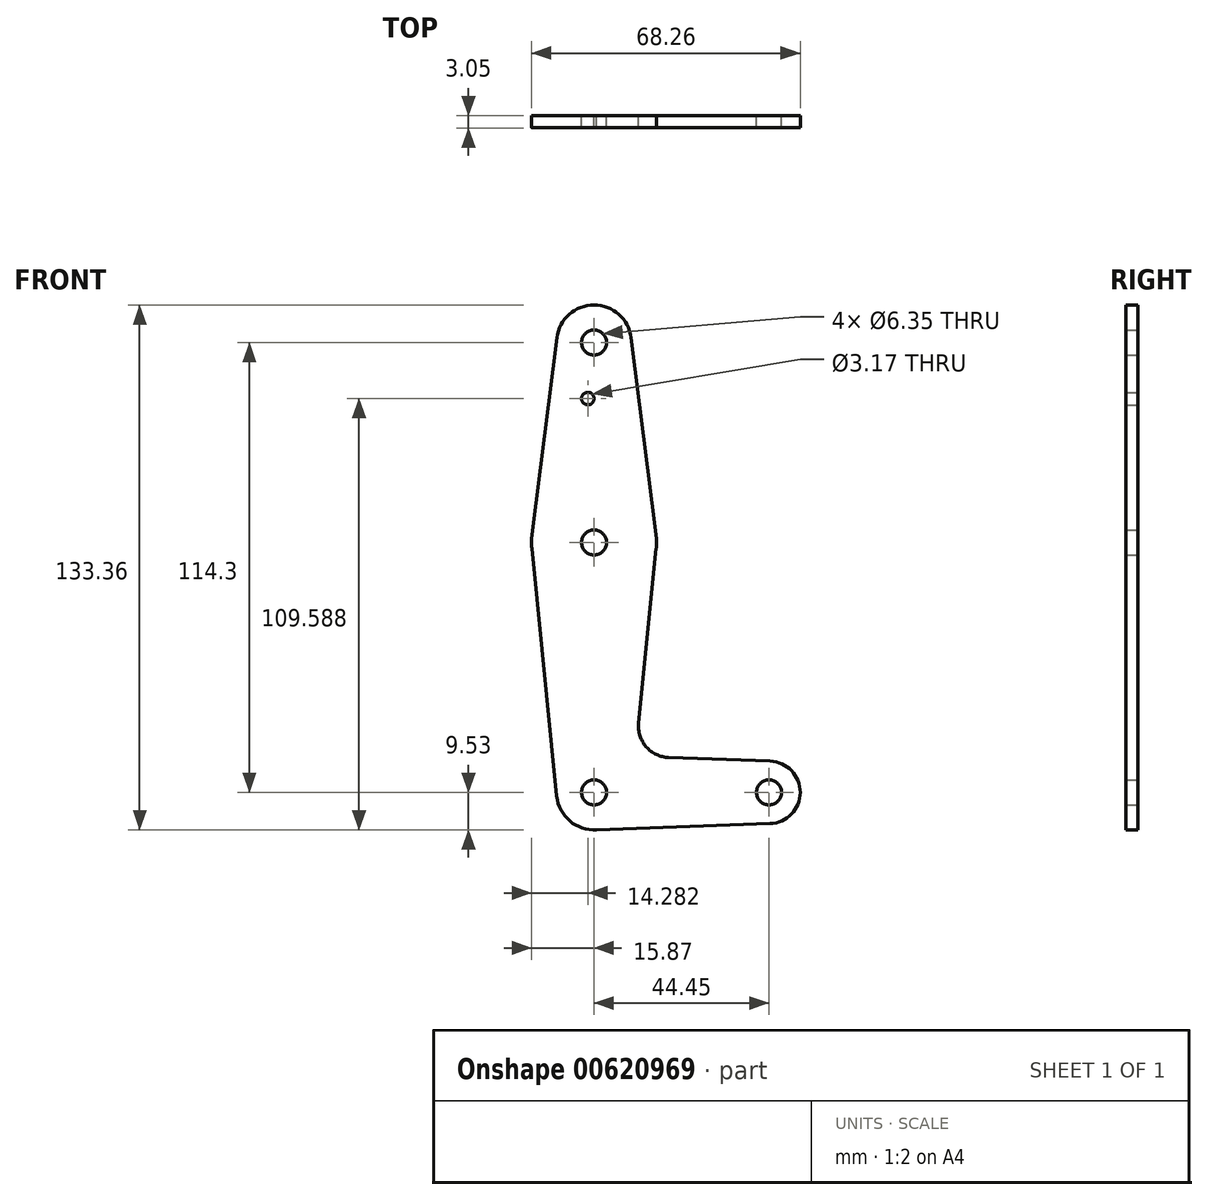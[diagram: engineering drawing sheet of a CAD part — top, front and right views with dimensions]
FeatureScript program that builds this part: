
annotation { "Feature Type Name" : "Feature", "Feature Type Description" : "" }
export const myFeature = defineFeature(function(context is Context, id is Id, definition is map)
    precondition{}
    {
        {
            var Q0;
            Q0=qCreatedBy(makeId("Front.planeOp"),FACE);
            var sketch = newSketch(context, id + "F0", { "sketchPlane" : qUnion([Q0])});
            skLineSegment(sketch, "E0", {"start": v(0, 0) * mm, "end": v(0, 114.3) * mm});
            skLineSegment(sketch, "E1", {"start": v(0, 114.3) * mm, "end": v(0, 0) * mm, "construction": true});
            skLineSegment(sketch, "E2", {"start": v(0, 0) * mm, "end": v(44.45, 0) * mm, "construction": true});
            skCircle(sketch, "E3", {"center": v(0, 0) * mm, "radius": 9.53 * mm});
            skCircle(sketch, "E4", {"center": v(0, 63.5) * mm, "radius": 15.88 * mm});
            skCircle(sketch, "E5", {"center": v(0, 114.3) * mm, "radius": 9.53 * mm});
            skCircle(sketch, "E6", {"center": v(44.45, 0) * mm, "radius": 7.94 * mm});
            skLineSegment(sketch, "E7", {"start": v(18.97, 8.85) * mm, "end": v(44.73, 7.93) * mm});
            skLineSegment(sketch, "E8", {"start": v(0, -9.53) * mm, "end": v(44.73, -7.93) * mm});
            skLineSegment(sketch, "E9", {"start": v(-15.8, 61.91) * mm, "end": v(-9.48, -0.95) * mm});
            skLineSegment(sketch, "E10", {"start": v(15.8, 61.91) * mm, "end": v(11.34, 17.59) * mm});
            skLineSegment(sketch, "E11", {"start": v(-15.75, 65.48) * mm, "end": v(-9.45, 115.5) * mm});
            skLineSegment(sketch, "E12", {"start": v(9.45, 115.5) * mm, "end": v(15.75, 65.48) * mm});
            skArc(sketch, "E13.filletArc", {"start": v(11.34, 17.59) * mm, "mid": v(13.26, 11.57) * mm, "end": v(18.97, 8.85) * mm});
            skCircle(sketch, "E14", {"center": v(0, 114.3) * mm, "radius": 3.18 * mm});
            skCircle(sketch, "E15", {"center": v(44.45, 0) * mm, "radius": 3.18 * mm});
            skCircle(sketch, "E16", {"center": v(0, 63.5) * mm, "radius": 3.18 * mm});
            skCircle(sketch, "E17", {"center": v(0, 0) * mm, "radius": 3.18 * mm});
            skCircle(sketch, "E18", {"center": v(-1.59, 100.06) * mm, "radius": 1.59 * mm});
            skSolve(sketch);
        }
        {
            var Q0;
            Q0 = qSketchRegion(id + "F0", true);
            extrude(context, id + "F1", {"entities" : qUnion([Q0]), "depth" : 3.05 * mm, "offsetDistance" : 25.4 * mm});
        }
    });
